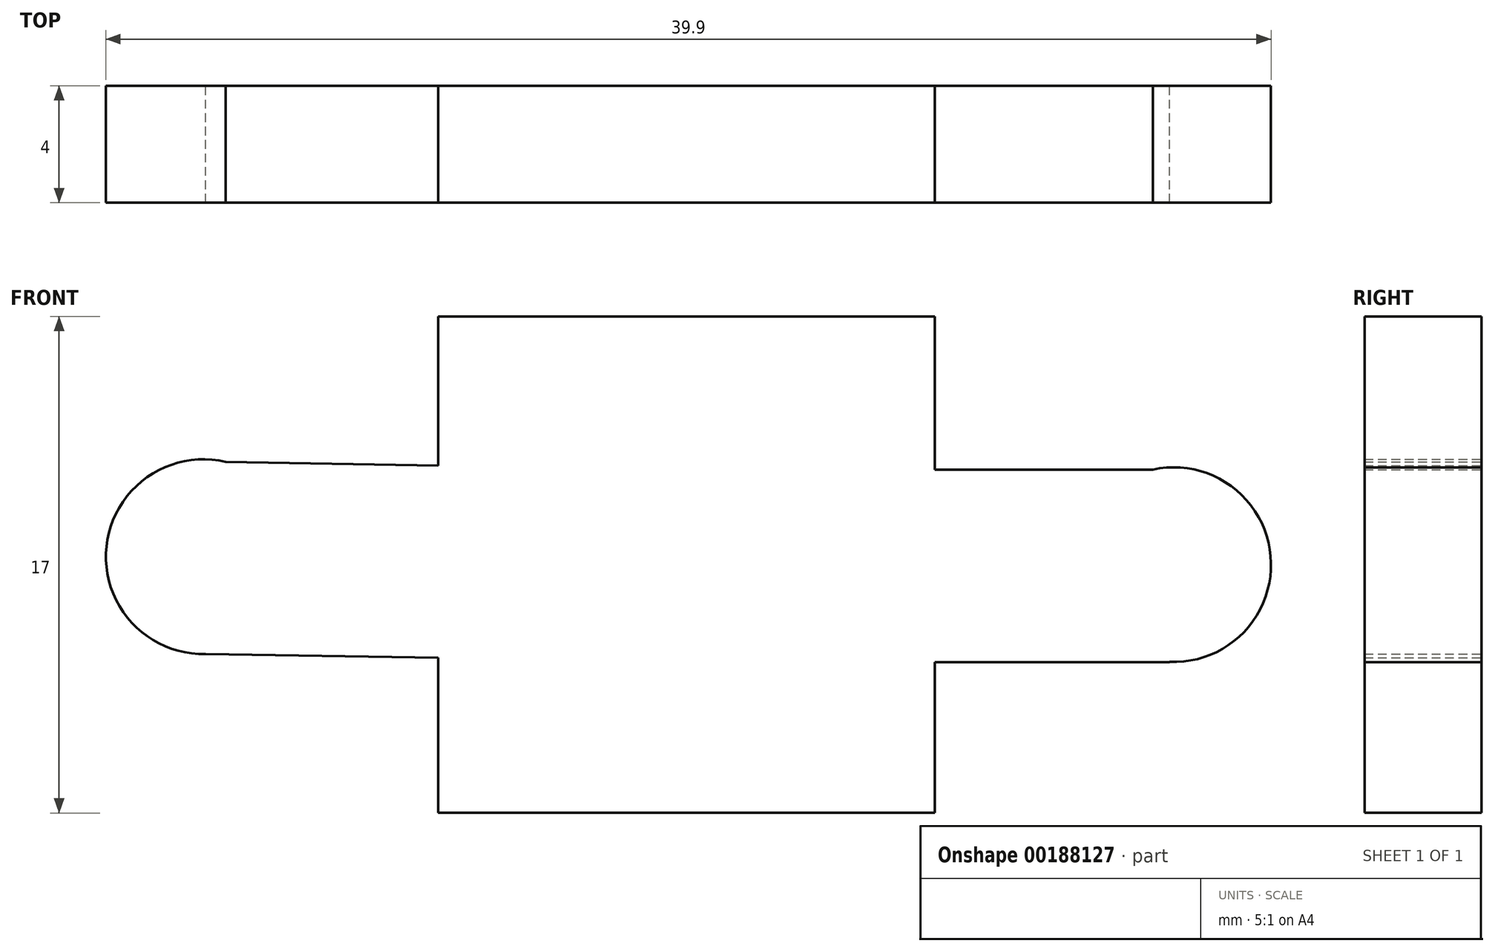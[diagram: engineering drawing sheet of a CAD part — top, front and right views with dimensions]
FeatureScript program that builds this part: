
annotation { "Feature Type Name" : "Feature", "Feature Type Description" : "" }
export const myFeature = defineFeature(function(context is Context, id is Id, definition is map)
    precondition{}
    {
        {
            var Q0;
            Q0=qCreatedBy(makeId("Front.planeOp"),FACE);
            var sketch = newSketch(context, id + "F0", { "sketchPlane" : qUnion([Q0])});
            skLineSegment(sketch, "E0", {"start": v(-8.64, 11.83) * mm, "end": v(8.36, 11.83) * mm});
            skLineSegment(sketch, "E1", {"start": v(8.36, 11.83) * mm, "end": v(8.36, -5.17) * mm});
            skLineSegment(sketch, "E2", {"start": v(8.36, -5.17) * mm, "end": v(-8.64, -5.17) * mm});
            skLineSegment(sketch, "E3", {"start": v(-8.64, -5.17) * mm, "end": v(-8.64, 11.83) * mm});
            skCircle(sketch, "E4", {"center": v(16.55, 3.33) * mm, "radius": 3.33 * mm});
            skPoint(sketch, "E4.centerSnap0", {"position": v(8.36, 3.33) * mm});
            skPoint(sketch, "E5.startSnap0", {"position": v(-0.14, 11.83) * mm});
            skPoint(sketch, "E5.endSnap0", {"position": v(-0.14, -5.17) * mm});
            skPoint(sketch, "E5.end.orphan", {"position": v(0, -5.17) * mm});
            skPoint(sketch, "E5.start.orphan", {"position": v(0, 11.83) * mm});
            skLineSegment(sketch, "E6", {"start": v(8.36, 6.59) * mm, "end": v(16.55, 6.59) * mm});
            skLineSegment(sketch, "E7", {"start": v(8.36, 0) * mm, "end": v(16.41, 0) * mm});
            skLineSegment(sketch, "E8", {"start": v(0, 11.83) * mm, "end": v(-0.14, -5.17) * mm});
            skLineSegment(sketch, "E9.MirrorCS", {"start": v(-8.45, 6.73) * mm, "end": v(-16.63, 6.86) * mm});
            skLineSegment(sketch, "E10.MirrorCS", {"start": v(-8.55, 0.14) * mm, "end": v(-16.6, 0.27) * mm});
            skCircle(sketch, "E11.MirrorC", {"center": v(-16.68, 3.6) * mm, "radius": 3.33 * mm});
            skLineSegment(sketch, "E12", {"start": v(-16.63, 6.86) * mm, "end": v(-16.6, 0.27) * mm});
            skLineSegment(sketch, "E13", {"start": v(16.55, 6.59) * mm, "end": v(16.41, 0) * mm});
            skSolve(sketch);
        }
        {
            var Q0;
            Q0 = qSketchRegion(id + "F0", true);
            extrude(context, id + "F1", {"entities" : qUnion([Q0]), "depth" : 4 * mm});
        }
    });
